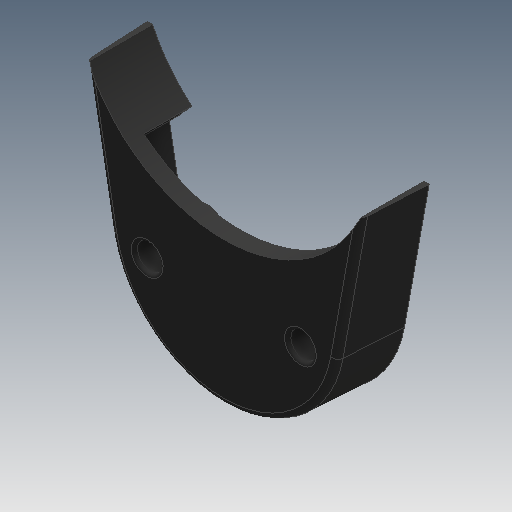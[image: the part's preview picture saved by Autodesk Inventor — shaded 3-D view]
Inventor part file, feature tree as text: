
AUTODESK INVENTOR PART (.ipt)
format: ipt  version: 2019 (Build 230136000, 136)  size: 284,672 bytes
history: native  units: mm
features: fillet x1
ambient origin geometry x8: Origin, YZ Plane, XZ Plane, XY Plane, X Axis, Y Axis, Z Axis, Center Point
bodies: Solid1 (feature_tree)
feature tree (1):
  fillet  "Fillet4"  [1 undecoded]
note: 1 required parameter value undecoded (feature->parameter linkage not recoverable at this tier; creation-order binding heuristic only, values carry confidence <= 0.55)
